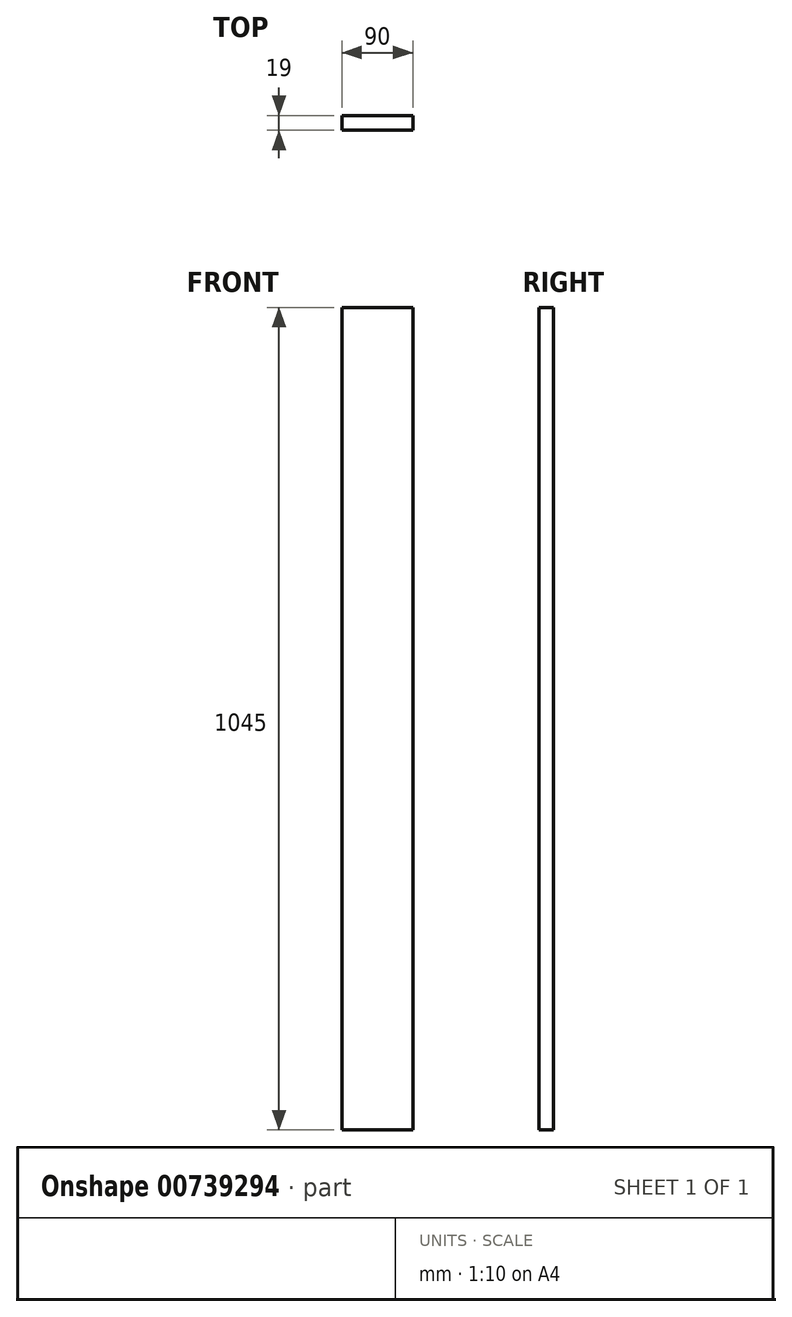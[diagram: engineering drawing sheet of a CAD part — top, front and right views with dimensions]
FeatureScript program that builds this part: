
annotation { "Feature Type Name" : "Feature", "Feature Type Description" : "" }
export const myFeature = defineFeature(function(context is Context, id is Id, definition is map)
    precondition{}
    {
        {
            var Q0;
            Q0=qCreatedBy(makeId("Top.planeOp"),FACE);
            var sketch = newSketch(context, id + "F0", { "sketchPlane" : qUnion([Q0])});
            skLineSegment(sketch, "E0.bottom", {"start": v(0, 0) * mm, "end": v(90, 0) * mm});
            skLineSegment(sketch, "E0.top", {"start": v(0, 19) * mm, "end": v(90, 19) * mm});
            skLineSegment(sketch, "E0.left", {"start": v(0, 0) * mm, "end": v(0, 19) * mm});
            skLineSegment(sketch, "E0.right", {"start": v(90, 0) * mm, "end": v(90, 19) * mm});
            skSolve(sketch);
        }
        {
            var Q0;
            Q0=makeQuery(id+"F0.imprint","IMPRINT",FACE,{"disambiguationData":[TD([[makeQuery(id+"F0.imprint","IMPRINT",EDGE,{"derivedFrom":sQuery(id+"F0.wireOp",EDGE,"E0.bottom")}),1.0]])]});
            extrude(context, id + "F1", {"entities" : qUnion([Q0]), "depth" : 1045 * mm, "offsetDistance" : 25 * mm});
        }
    });
